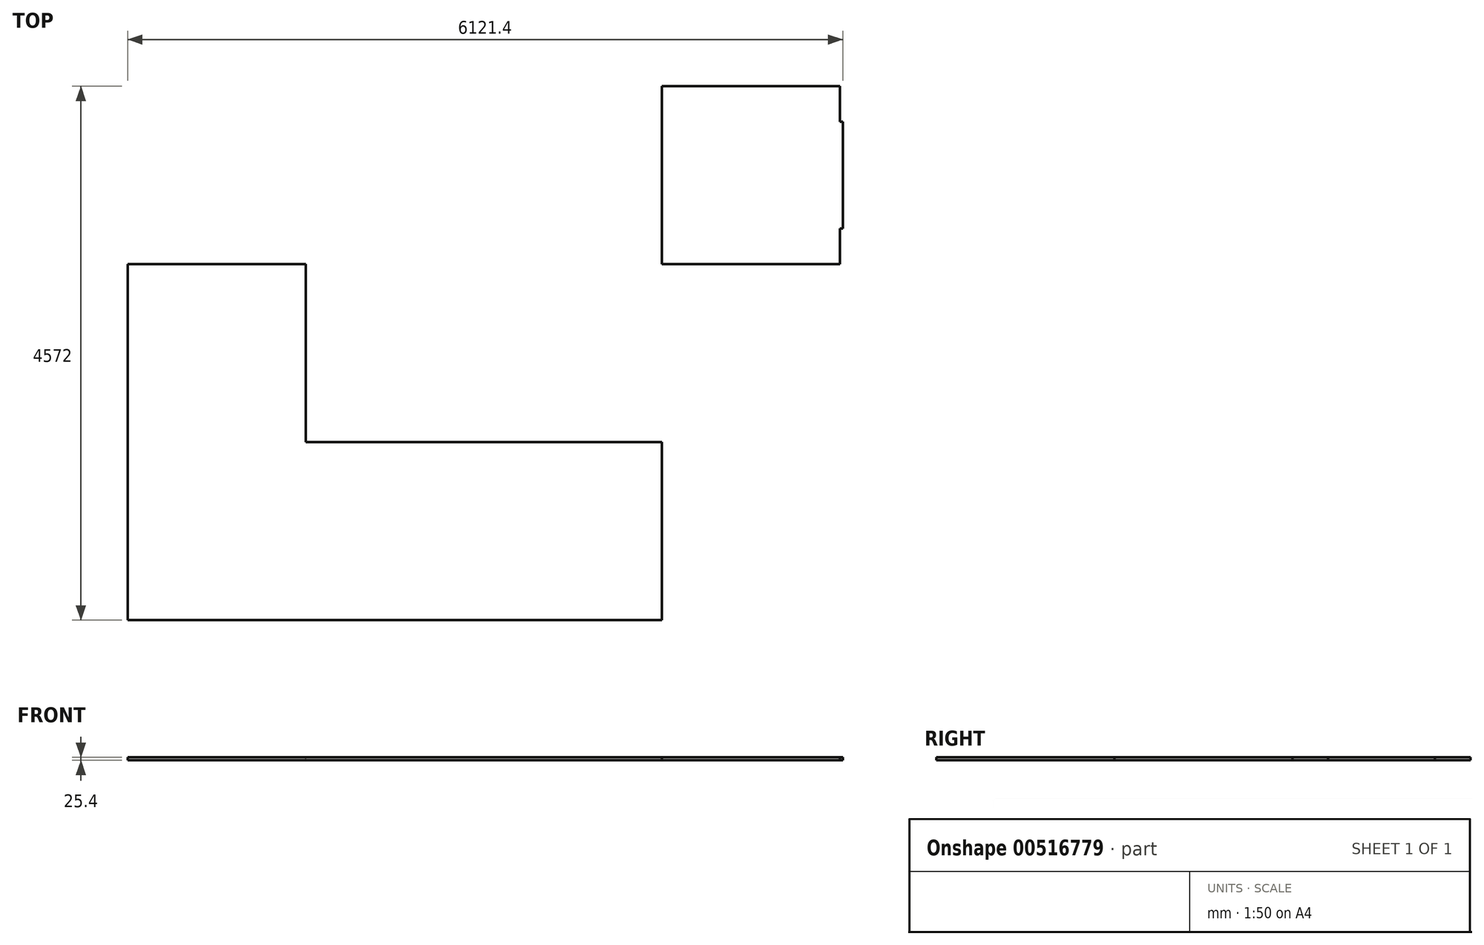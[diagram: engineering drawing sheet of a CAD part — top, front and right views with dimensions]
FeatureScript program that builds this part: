
annotation { "Feature Type Name" : "Feature", "Feature Type Description" : "" }
export const myFeature = defineFeature(function(context is Context, id is Id, definition is map)
    precondition{}
    {
        {
            var Q0;
            Q0=qCreatedBy(makeId("Top.planeOp"),FACE);
            var sketch = newSketch(context, id + "F0", { "sketchPlane" : qUnion([Q0])});
            skLineSegment(sketch, "E0.bottom", {"start": v(0, 0) * mm, "end": v(1524, 0) * mm});
            skLineSegment(sketch, "E0.top", {"start": v(0, -1524) * mm, "end": v(1524, -1524) * mm});
            skLineSegment(sketch, "E0.left", {"start": v(0, 0) * mm, "end": v(0, -1524) * mm});
            skLineSegment(sketch, "E0.right", {"start": v(1524, 0) * mm, "end": v(1524, -1524) * mm});
            skLineSegment(sketch, "E1.0.1.1", {"start": v(1524, 1524) * mm, "end": v(1524, 0) * mm});
            skLineSegment(sketch, "E1.0.1.2", {"start": v(0, 1524) * mm, "end": v(0, 0) * mm});
            skLineSegment(sketch, "E1.0.1.3", {"start": v(0, 1524) * mm, "end": v(1524, 1524) * mm});
            skLineSegment(sketch, "E1.0.2.0", {"start": v(0, 1524) * mm, "end": v(1524, 1524) * mm});
            skLineSegment(sketch, "E1.0.2.1", {"start": v(1524, 3048) * mm, "end": v(1524, 1524) * mm});
            skLineSegment(sketch, "E1.0.2.2", {"start": v(0, 3048) * mm, "end": v(0, 1524) * mm});
            skLineSegment(sketch, "E1.0.2.3", {"start": v(0, 3048) * mm, "end": v(1524, 3048) * mm});
            skLineSegment(sketch, "E1.0.3.0", {"start": v(0, 3048) * mm, "end": v(1524, 3048) * mm});
            skLineSegment(sketch, "E1.0.3.1", {"start": v(1524, 4572) * mm, "end": v(1524, 3048) * mm});
            skLineSegment(sketch, "E1.0.3.2", {"start": v(0, 4572) * mm, "end": v(0, 3048) * mm});
            skLineSegment(sketch, "E1.0.3.3", {"start": v(0, 4572) * mm, "end": v(1524, 4572) * mm});
            skLineSegment(sketch, "E1.1.0.0", {"start": v(1524, -1524) * mm, "end": v(3048, -1524) * mm});
            skLineSegment(sketch, "E1.1.0.1", {"start": v(3048, 0) * mm, "end": v(3048, -1524) * mm});
            skLineSegment(sketch, "E1.1.0.3", {"start": v(1524, 0) * mm, "end": v(3048, 0) * mm});
            skLineSegment(sketch, "E1.1.1.0", {"start": v(1524, 0) * mm, "end": v(3048, 0) * mm});
            skLineSegment(sketch, "E1.1.1.1", {"start": v(3048, 1524) * mm, "end": v(3048, 0) * mm});
            skLineSegment(sketch, "E1.1.1.2", {"start": v(1524, 1524) * mm, "end": v(1524, 0) * mm});
            skLineSegment(sketch, "E1.1.1.3", {"start": v(1524, 1524) * mm, "end": v(3048, 1524) * mm});
            skLineSegment(sketch, "E1.1.2.0", {"start": v(1524, 1524) * mm, "end": v(3048, 1524) * mm});
            skLineSegment(sketch, "E1.1.2.1", {"start": v(3048, 3048) * mm, "end": v(3048, 1524) * mm});
            skLineSegment(sketch, "E1.1.2.2", {"start": v(1524, 3048) * mm, "end": v(1524, 1524) * mm});
            skLineSegment(sketch, "E1.1.2.3", {"start": v(1524, 3048) * mm, "end": v(3048, 3048) * mm});
            skLineSegment(sketch, "E1.1.3.0", {"start": v(1524, 3048) * mm, "end": v(3048, 3048) * mm});
            skLineSegment(sketch, "E1.1.3.1", {"start": v(3048, 4572) * mm, "end": v(3048, 3048) * mm});
            skLineSegment(sketch, "E1.1.3.2", {"start": v(1524, 4572) * mm, "end": v(1524, 3048) * mm});
            skLineSegment(sketch, "E1.1.3.3", {"start": v(1524, 4572) * mm, "end": v(3048, 4572) * mm});
            skLineSegment(sketch, "E1.2.0.0", {"start": v(3048, -1524) * mm, "end": v(4572, -1524) * mm});
            skLineSegment(sketch, "E1.2.0.1", {"start": v(4572, 0) * mm, "end": v(4572, -1524) * mm});
            skLineSegment(sketch, "E1.2.0.2", {"start": v(3048, 0) * mm, "end": v(3048, -1524) * mm});
            skLineSegment(sketch, "E1.2.0.3", {"start": v(3048, 0) * mm, "end": v(4572, 0) * mm});
            skLineSegment(sketch, "E1.2.1.0", {"start": v(3048, 0) * mm, "end": v(4572, 0) * mm});
            skLineSegment(sketch, "E1.2.1.1", {"start": v(4572, 1524) * mm, "end": v(4572, 0) * mm});
            skLineSegment(sketch, "E1.2.1.2", {"start": v(3048, 1524) * mm, "end": v(3048, 0) * mm});
            skLineSegment(sketch, "E1.2.1.3", {"start": v(3048, 1524) * mm, "end": v(4572, 1524) * mm});
            skLineSegment(sketch, "E1.2.2.0", {"start": v(3048, 1524) * mm, "end": v(4572, 1524) * mm});
            skLineSegment(sketch, "E1.2.2.1", {"start": v(4572, 3048) * mm, "end": v(4572, 1524) * mm});
            skLineSegment(sketch, "E1.2.2.2", {"start": v(3048, 3048) * mm, "end": v(3048, 1524) * mm});
            skLineSegment(sketch, "E1.2.2.3", {"start": v(3048, 3048) * mm, "end": v(4572, 3048) * mm});
            skLineSegment(sketch, "E1.2.3.0", {"start": v(3048, 3048) * mm, "end": v(4572, 3048) * mm});
            skLineSegment(sketch, "E1.2.3.1", {"start": v(4572, 4572) * mm, "end": v(4572, 3048) * mm});
            skLineSegment(sketch, "E1.2.3.2", {"start": v(3048, 4572) * mm, "end": v(3048, 3048) * mm});
            skLineSegment(sketch, "E1.2.3.3", {"start": v(3048, 4572) * mm, "end": v(4572, 4572) * mm});
            skLineSegment(sketch, "E1.direction1", {"start": v(0, -1524) * mm, "end": v(1524, -1524) * mm, "construction": true});
            skLineSegment(sketch, "E1.direction2", {"start": v(0, -1524) * mm, "end": v(0, 0) * mm, "construction": true});
            skLineSegment(sketch, "E2.bottom", {"start": v(4572, 3048) * mm, "end": v(6096, 3048) * mm});
            skLineSegment(sketch, "E2.top", {"start": v(4572, 1524) * mm, "end": v(6096, 1524) * mm});
            skLineSegment(sketch, "E2.right", {"start": v(6096, 3048) * mm, "end": v(6096, 1524) * mm});
            skSolve(sketch);
        }
        {
            var Q0;
            Q0=makeQuery(id+"F0.imprint","IMPRINT",FACE,{"disambiguationData":[TD([[makeQuery(id+"F0.imprint","IMPRINT",EDGE,{"derivedFrom":sQuery(id+"F0.wireOp",EDGE,"E2.bottom")}),-1.0]])]});
            var Q1;
            Q1=makeQuery(id+"F0.imprint","IMPRINT",FACE,{"disambiguationData":[TD([[makeQuery(id+"F0.imprint","IMPRINT",EDGE,{"derivedFrom":sQuery(id+"F0.wireOp",EDGE,"E0.top")}),1.0]])]});
            var Q2;
            Q2=makeQuery(id+"F0.imprint","IMPRINT",FACE,{"disambiguationData":[TD([[makeQuery(id+"F0.imprint","IMPRINT",EDGE,{"derivedFrom":sQuery(id+"F0.wireOp",EDGE,"E1.0.3.0")}),1.0]])]});
            var Q3;
            Q3=makeQuery(id+"F0.imprint","IMPRINT",FACE,{"disambiguationData":[TD([[makeQuery(id+"F0.imprint","IMPRINT",EDGE,{"derivedFrom":sQuery(id+"F0.wireOp",EDGE,"E1.2.0.0")}),1.0]])]});
            var Q4;
            Q4=makeQuery(id+"F0.imprint","IMPRINT",FACE,{"disambiguationData":[TD([[makeQuery(id+"F0.imprint","IMPRINT",EDGE,{"derivedFrom":sQuery(id+"F0.wireOp",EDGE,"E1.2.3.0")}),1.0]])]});
            var Q5;
            Q5=makeQuery(id+"F0.imprint","IMPRINT",FACE,{"disambiguationData":[TD([[makeQuery(id+"F0.imprint","IMPRINT",EDGE,{"derivedFrom":sQuery(id+"F0.wireOp",EDGE,"E0.bottom")}),1.0]])]});
            var Q6;
            Q6=makeQuery(id+"F0.imprint","IMPRINT",FACE,{"disambiguationData":[TD([[makeQuery(id+"F0.imprint","IMPRINT",EDGE,{"derivedFrom":sQuery(id+"F0.wireOp",EDGE,"E1.0.2.0")}),1.0]])]});
            var Q7;
            Q7=makeQuery(id+"F0.imprint","IMPRINT",FACE,{"disambiguationData":[TD([[makeQuery(id+"F0.imprint","IMPRINT",EDGE,{"derivedFrom":sQuery(id+"F0.wireOp",EDGE,"E1.1.0.0")}),1.0]])]});
            var Q8;
            Q8=makeQuery(id+"F0.imprint","IMPRINT",FACE,{"disambiguationData":[TD([[makeQuery(id+"F0.imprint","IMPRINT",EDGE,{"derivedFrom":sQuery(id+"F0.wireOp",EDGE,"E1.1.3.0")}),1.0]])]});
            var Q9;
            Q9=makeQuery(id+"F0.imprint","IMPRINT",FACE,{"disambiguationData":[TD([[makeQuery(id+"F0.imprint","IMPRINT",EDGE,{"derivedFrom":sQuery(id+"F0.wireOp",EDGE,"E1.2.1.0")}),1.0]])]});
            var Q10;
            Q10=makeQuery(id+"F0.imprint","IMPRINT",FACE,{"disambiguationData":[TD([[makeQuery(id+"F0.imprint","IMPRINT",EDGE,{"derivedFrom":sQuery(id+"F0.wireOp",EDGE,"E1.1.1.0")}),1.0]])]});
            var Q11;
            Q11=makeQuery(id+"F0.imprint","IMPRINT",FACE,{"disambiguationData":[TD([[makeQuery(id+"F0.imprint","IMPRINT",EDGE,{"derivedFrom":sQuery(id+"F0.wireOp",EDGE,"E1.1.2.0")}),1.0]])]});
            var Q12;
            Q12=makeQuery(id+"F0.imprint","IMPRINT",FACE,{"disambiguationData":[TD([[makeQuery(id+"F0.imprint","IMPRINT",EDGE,{"derivedFrom":sQuery(id+"F0.wireOp",EDGE,"E1.2.2.0")}),1.0]])]});
            extrude(context, id + "F1", {"entities" : qUnion([Q0, Q1, Q2, Q3, Q4, Q5, Q6, Q7, Q8, Q9, Q10, Q11, Q12]), "depth" : -25.4 * mm, "offsetDistance" : 25.4 * mm});
        }
        {
            var Q0;
            Q0=makeQuery(id+"F1.opExtrude","SWEPT_FACE",FACE,{"disambiguationData":[OSD([sQuery(id+"F0.wireOp",EDGE,"E2.right")])]});
            var sketch = newSketch(context, id + "F2", { "sketchPlane" : qUnion([Q0])});
            skLineSegment(sketch, "E3.bottom", {"start": v(2743.2, -25.4) * mm, "end": v(1828.8, -25.4) * mm});
            skLineSegment(sketch, "E3.top", {"start": v(2743.2, 0) * mm, "end": v(1828.8, 0) * mm});
            skLineSegment(sketch, "E3.left", {"start": v(2743.2, -25.4) * mm, "end": v(2743.2, 0) * mm});
            skLineSegment(sketch, "E3.right", {"start": v(1828.8, -25.4) * mm, "end": v(1828.8, 0) * mm});
            skSolve(sketch);
        }
        {
            var Q0;
            Q0=makeQuery(id+"F2.imprint","IMPRINT",FACE,{"disambiguationData":[TD([[makeQuery(id+"F2.imprint","IMPRINT",EDGE,{"derivedFrom":sQuery(id+"F2.wireOp",EDGE,"E3.bottom")}),-1.0]])]});
            extrude(context, id + "F3", {"entities" : qUnion([Q0]), "operationType" : NewBodyOperationType.ADD, "depth" : 25.4 * mm, "offsetDistance" : 25.4 * mm});
        }
    });
